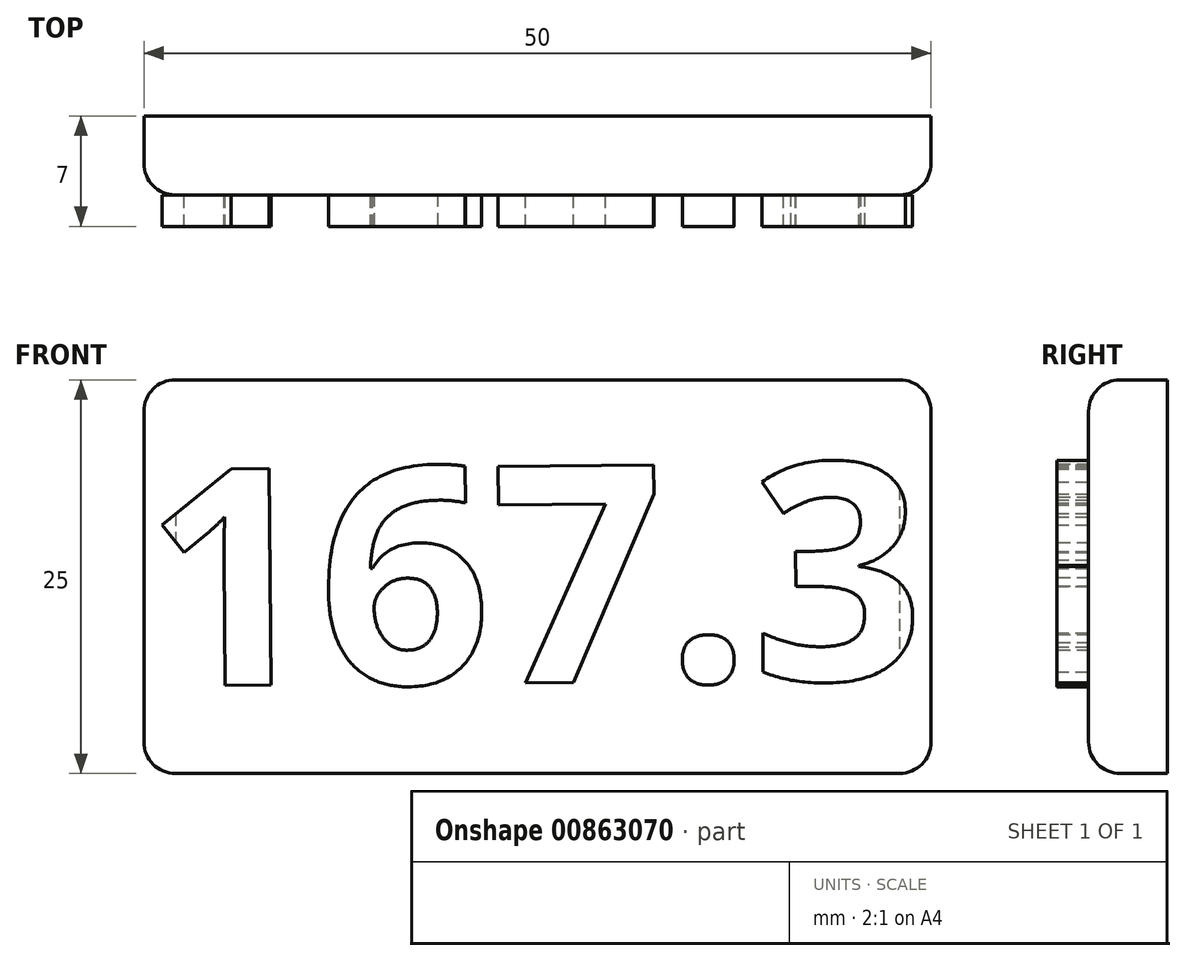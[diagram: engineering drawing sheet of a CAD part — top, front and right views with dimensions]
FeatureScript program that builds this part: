
annotation { "Feature Type Name" : "Feature", "Feature Type Description" : "" }
export const myFeature = defineFeature(function(context is Context, id is Id, definition is map)
    precondition{}
    {
        {
            var Q0;
            Q0=qCreatedBy(makeId("Front.planeOp"),FACE);
            var sketch = newSketch(context, id + "F0", { "sketchPlane" : qUnion([Q0])});
            skLineSegment(sketch, "E0.bottom", {"start": v(25, 12.5) * mm, "end": v(-25, 12.5) * mm});
            skLineSegment(sketch, "E0.top", {"start": v(25, -12.5) * mm, "end": v(-25, -12.5) * mm});
            skLineSegment(sketch, "E0.left", {"start": v(25, 12.5) * mm, "end": v(25, -12.5) * mm});
            skLineSegment(sketch, "E0.right", {"start": v(-25, 12.5) * mm, "end": v(-25, -12.5) * mm});
            skPoint(sketch, "E0.middle", {"position": v(0, 0) * mm});
            skSolve(sketch);
        }
        {
            var Q0;
            Q0=makeQuery(id+"F0.imprint","IMPRINT",FACE,{"disambiguationData":[TD([[makeQuery(id+"F0.imprint","IMPRINT",EDGE,{"derivedFrom":sQuery(id+"F0.wireOp",EDGE,"E0.bottom")}),1.0]])]});
            extrude(context, id + "F1", {"entities" : qUnion([Q0]), "depth" : 5 * mm, "offsetDistance" : 25 * mm});
        }
        {
            var Q0;
            Q0=makeQuery(id+"F1.opExtrude","CAP_FACE",FACE,{"disambiguationData":[OSD([sQuery(id+"F0.wireOp",EDGE,"E0.bottom"),sQuery(id+"F0.wireOp",EDGE,"E0.top"),sQuery(id+"F0.wireOp",EDGE,"E0.left"),sQuery(id+"F0.wireOp",EDGE,"E0.right")])],"isStart":false});
            var sketch = newSketch(context, id + "F2", { "sketchPlane" : qUnion([Q0])});
            skText(sketch, "E1", { "text": "167.3\n", "fontName": "OpenSans-Bold.ttf"});
            const initialGuessF2  = {"E1": [-0.0249, -0.00696, 0.99996, 0.00898, 0.01388]};
            skSetInitialGuess(sketch, initialGuessF2);
            skSolve(sketch);
        }
        {
            var Q0;
            Q0=makeQuery(id+"F1.opExtrude","CAP_FACE",FACE,{"disambiguationData":[OSD([sQuery(id+"F0.wireOp",EDGE,"E0.bottom"),sQuery(id+"F0.wireOp",EDGE,"E0.top"),sQuery(id+"F0.wireOp",EDGE,"E0.left"),sQuery(id+"F0.wireOp",EDGE,"E0.right")])],"isStart":false});
            var Q1;
            Q1=makeQuery(id+"F1.opExtrude","SWEPT_EDGE",EDGE,{"disambiguationData":[OSD([sQuery(id+"F0.wireOp",EDGE,"E0.bottom"),sQuery(id+"F0.wireOp",EDGE,"E0.right")])]});
            var Q2;
            Q2=makeQuery(id+"F1.opExtrude","SWEPT_EDGE",EDGE,{"disambiguationData":[OSD([sQuery(id+"F0.wireOp",EDGE,"E0.bottom"),sQuery(id+"F0.wireOp",EDGE,"E0.left")])]});
            var Q3;
            Q3=makeQuery(id+"F1.opExtrude","SWEPT_EDGE",EDGE,{"disambiguationData":[OSD([sQuery(id+"F0.wireOp",EDGE,"E0.top"),sQuery(id+"F0.wireOp",EDGE,"E0.left")])]});
            var Q4;
            Q4=makeQuery(id+"F1.opExtrude","SWEPT_EDGE",EDGE,{"disambiguationData":[OSD([sQuery(id+"F0.wireOp",EDGE,"E0.top"),sQuery(id+"F0.wireOp",EDGE,"E0.right")])]});
            fillet(context, id + "F3", {"entities" : qUnion([Q0, Q1, Q2, Q3, Q4]), "radius" : 2 * mm, "tangentPropagation" : true, "allowEdgeOverflow" : false});
        }
        {
            var Q0;
            Q0 = qSketchRegion(id + "F2", true);
            extrude(context, id + "F4", {"entities" : qUnion([Q0]), "operationType" : NewBodyOperationType.ADD, "depth" : 2 * mm, "offsetDistance" : 25 * mm});
        }
    });
